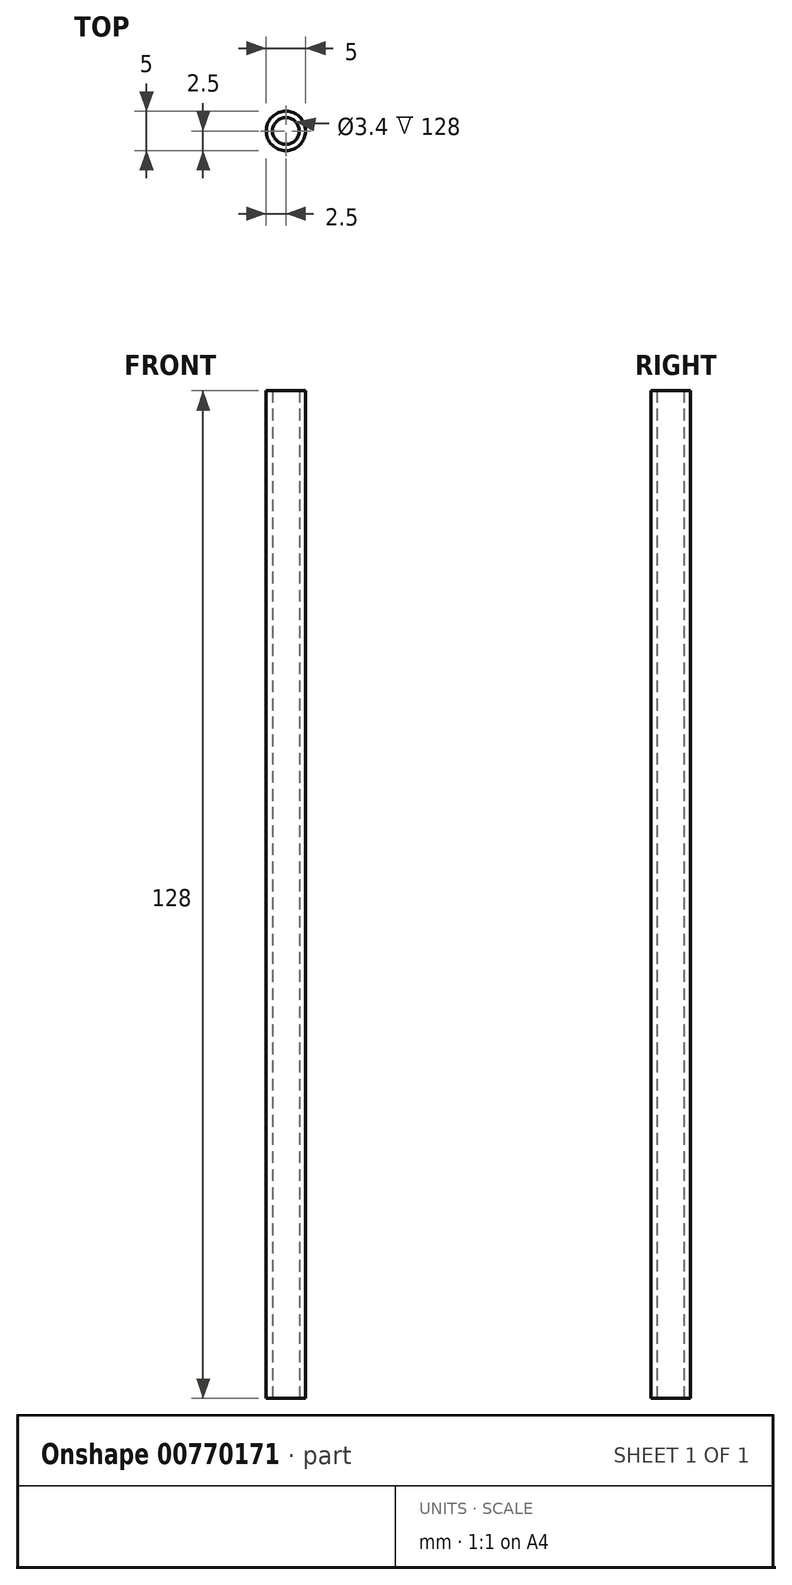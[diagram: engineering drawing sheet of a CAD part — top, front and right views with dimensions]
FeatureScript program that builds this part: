
annotation { "Feature Type Name" : "Feature", "Feature Type Description" : "" }
export const myFeature = defineFeature(function(context is Context, id is Id, definition is map)
    precondition{}
    {
        {
            var Q0;
            Q0=qCreatedBy(makeId("Top.planeOp"),FACE);
            var sketch = newSketch(context, id + "F0", { "sketchPlane" : qUnion([Q0])});
            skCircle(sketch, "E0", {"center": v(0, 0) * mm, "radius": 2.5 * mm});
            skCircle(sketch, "E1", {"center": v(0, 0) * mm, "radius": 1.7 * mm});
            skSolve(sketch);
        }
        {
            var Q0;
            Q0 = qSketchRegion(id + "F0", true);
            extrude(context, id + "F1", {"entities" : qUnion([Q0]), "depth" : 128 * mm, "offsetDistance" : 25 * mm});
        }
    });
